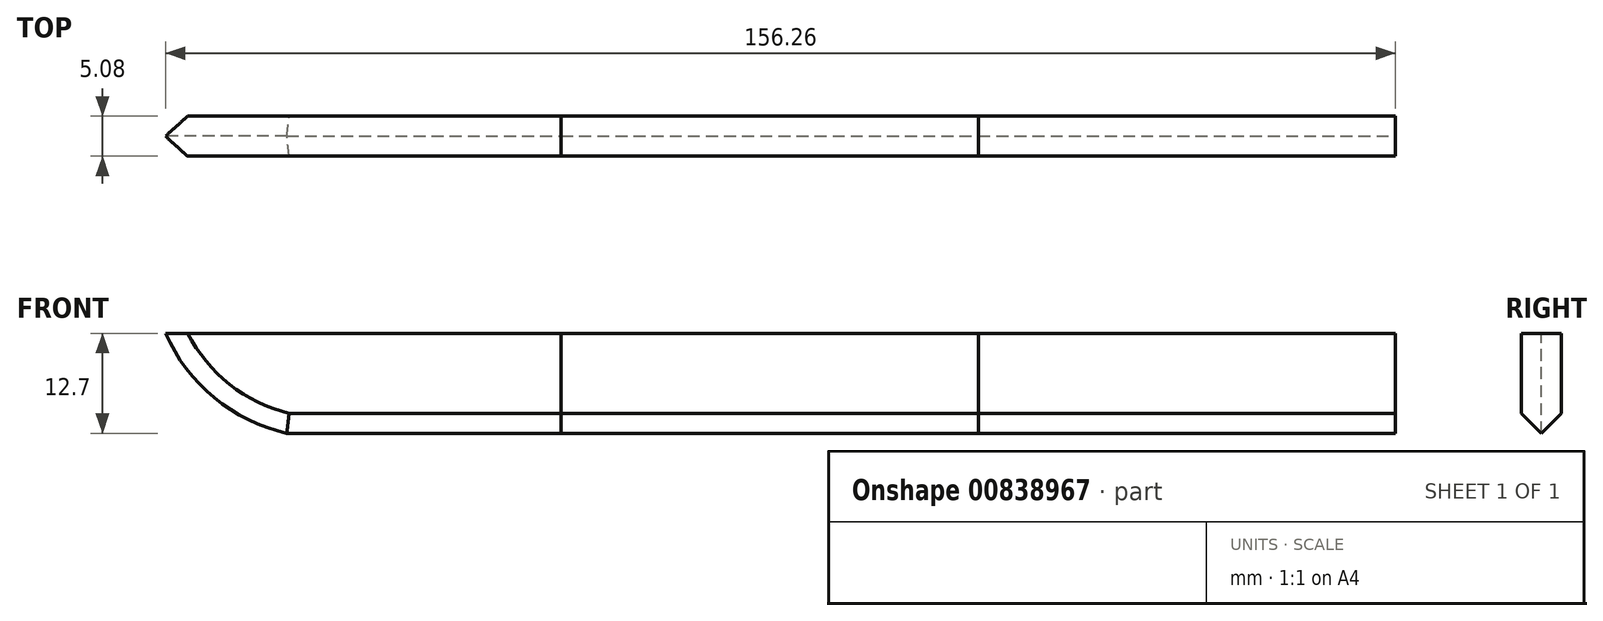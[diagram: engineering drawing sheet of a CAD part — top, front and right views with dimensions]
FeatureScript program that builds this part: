
annotation { "Feature Type Name" : "Feature", "Feature Type Description" : "" }
export const myFeature = defineFeature(function(context is Context, id is Id, definition is map)
    precondition{}
    {
        {
            var Q0;
            Q0=qCreatedBy(makeId("Front.planeOp"),FACE);
            var sketch = newSketch(context, id + "F0", { "sketchPlane" : qUnion([Q0])});
            skLineSegment(sketch, "E0.bottom", {"start": v(26.5, -7.62) * mm, "end": v(-26.5, -7.62) * mm});
            skLineSegment(sketch, "E0.top", {"start": v(26.5, 7.62) * mm, "end": v(-26.5, 7.62) * mm});
            skLineSegment(sketch, "E0.left", {"start": v(26.5, -7.62) * mm, "end": v(26.5, 7.62) * mm});
            skLineSegment(sketch, "E0.right", {"start": v(-26.5, -7.62) * mm, "end": v(-26.5, 7.62) * mm});
            skPoint(sketch, "E0.middle", {"position": v(0, 0) * mm});
            skSolve(sketch);
        }
        {
            var Q0;
            Q0 = qSketchRegion(id + "F0", true);
            extrude(context, id + "F1", {"entities" : qUnion([Q0]), "depth" : 2.54 * mm, "offsetDistance" : 25.4 * mm, "hasSecondDirection" : true, "secondDirectionOppositeDirection" : true, "secondDirectionDepth" : 2.54 * mm});
        }
        {
            var Q0;
            Q0=qCreatedBy(makeId("Front.planeOp"),FACE);
            var sketch = newSketch(context, id + "F2", { "sketchPlane" : qUnion([Q0])});
            skLineSegment(sketch, "E1.bottom", {"start": v(-26.52, -7.62) * mm, "end": v(-61.63, -7.62) * mm});
            skLineSegment(sketch, "E1.top", {"start": v(-26.52, 7.62) * mm, "end": v(-79.21, 7.62) * mm});
            skLineSegment(sketch, "E1.left", {"start": v(-26.52, -7.62) * mm, "end": v(-26.52, 7.62) * mm});
            skPoint(sketch, "E1.middle", {"position": v(-53.02, 0) * mm});
            skArc(sketch, "E2", {"start": v(-79.21, 6.87) * mm, "mid": v(-72.18, -2.5) * mm, "end": v(-61.63, -7.62) * mm});
            skLineSegment(sketch, "E3", {"start": v(-79.21, 7.62) * mm, "end": v(-79.21, 6.87) * mm});
            skPoint(sketch, "E4.orphan", {"position": v(-79.52, 7.62) * mm});
            skPoint(sketch, "E5.orphan", {"position": v(-79.52, -7.62) * mm});
            skSolve(sketch);
        }
        {
            var Q0;
            Q0 = qSketchRegion(id + "F2", true);
            extrude(context, id + "F3", {"entities" : qUnion([Q0]), "depth" : 2.54 * mm, "offsetDistance" : 25.4 * mm, "hasSecondDirection" : true, "secondDirectionOppositeDirection" : true, "secondDirectionDepth" : 2.54 * mm});
        }
        {
            var Q0;
            Q0=qCreatedBy(makeId("Front.planeOp"),FACE);
            var sketch = newSketch(context, id + "F4", { "sketchPlane" : qUnion([Q0])});
            skLineSegment(sketch, "E6.bottom", {"start": v(79.5, -7.62) * mm, "end": v(26.5, -7.62) * mm});
            skLineSegment(sketch, "E6.top", {"start": v(79.5, 7.62) * mm, "end": v(26.5, 7.62) * mm});
            skLineSegment(sketch, "E6.left", {"start": v(79.5, -7.62) * mm, "end": v(79.5, 7.62) * mm});
            skLineSegment(sketch, "E6.right", {"start": v(26.5, -7.62) * mm, "end": v(26.5, 7.62) * mm});
            skPoint(sketch, "E6.middle", {"position": v(53, 0) * mm});
            skSolve(sketch);
        }
        {
            var Q0;
            Q0 = qSketchRegion(id + "F4", true);
            extrude(context, id + "F5", {"entities" : qUnion([Q0]), "depth" : 2.54 * mm, "offsetDistance" : 25.4 * mm, "hasSecondDirection" : true, "secondDirectionOppositeDirection" : true, "secondDirectionDepth" : 2.54 * mm});
        }
        {
            var Q0;
            Q0=makeQuery(id+"F3.opExtrude","CAP_EDGE",EDGE,{"disambiguationData":[OSD([sQuery(id+"F2.wireOp",EDGE,"E1.bottom")])],"isStart":false});
            var Q1;
            Q1=makeQuery(id+"F3.opExtrude","CAP_EDGE",EDGE,{"disambiguationData":[OSD([sQuery(id+"F2.wireOp",EDGE,"E1.bottom")])],"isStart":true});
            var Q2;
            Q2=makeQuery(id+"F1.opExtrude","CAP_EDGE",EDGE,{"disambiguationData":[OSD([sQuery(id+"F0.wireOp",EDGE,"E0.bottom")])],"isStart":false});
            var Q3;
            Q3=makeQuery(id+"F1.opExtrude","CAP_EDGE",EDGE,{"disambiguationData":[OSD([sQuery(id+"F0.wireOp",EDGE,"E0.bottom")])],"isStart":true});
            var Q4;
            Q4=makeQuery(id+"F5.opExtrude","CAP_EDGE",EDGE,{"disambiguationData":[OSD([sQuery(id+"F4.wireOp",EDGE,"E6.bottom")])],"isStart":true});
            var Q5;
            Q5=makeQuery(id+"F5.opExtrude","CAP_EDGE",EDGE,{"disambiguationData":[OSD([sQuery(id+"F4.wireOp",EDGE,"E6.bottom")])],"isStart":false});
            chamfer(context, id + "F6", {"entities" : qUnion([Q0, Q1, Q2, Q3, Q4, Q5]), "width" : 5.08 * mm, "tangentPropagation" : true});
        }
        {
            var Q0;
            Q0=makeQuery(id+"F3.opExtrude","CAP_EDGE",EDGE,{"disambiguationData":[OSD([sQuery(id+"F2.wireOp",EDGE,"E2")])],"isStart":false});
            var Q1;
            Q1=makeQuery(id+"F3.opExtrude","CAP_EDGE",EDGE,{"disambiguationData":[OSD([sQuery(id+"F2.wireOp",EDGE,"E2")])],"isStart":true});
            chamfer(context, id + "F7", {"entities" : qUnion([Q0, Q1]), "width" : 5.08 * mm, "tangentPropagation" : true});
        }
    });
